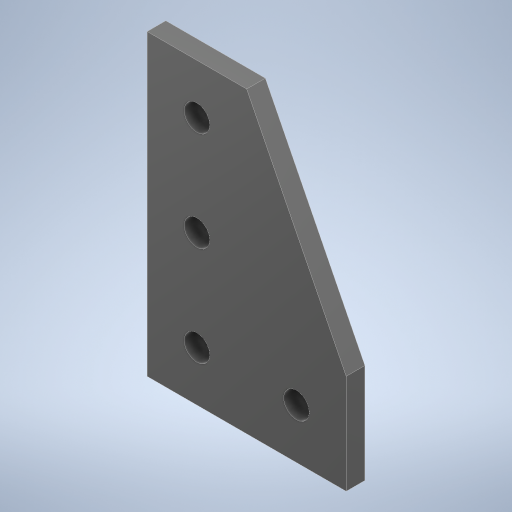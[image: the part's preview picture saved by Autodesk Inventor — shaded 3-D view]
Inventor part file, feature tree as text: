
AUTODESK INVENTOR PART (.ipt)
format: ipt  version: 2024 (Build 280153000, 153)  size: 271,360 bytes
history: native  units: in
note: dims shown in document units (in); Inventor stores cm internally (conversion verified against a paired STEP export)
features: extrude x1, sketch x1, other x1
ambient origin geometry x8: Origin, YZ Plane, XZ Plane, XY Plane, X Axis, Y Axis, Z Axis, Center Point
bodies: Solid1 (feature_tree)
feature tree (3):
  extrude  "Extrusion2"  Depth=2.0in
  sketch  "Sketch2"  dims[d7=2.0in d8=2.0in d9=1.0in d10=1.0in d11=0.0in]
  other  "Boss-Extrude1"
